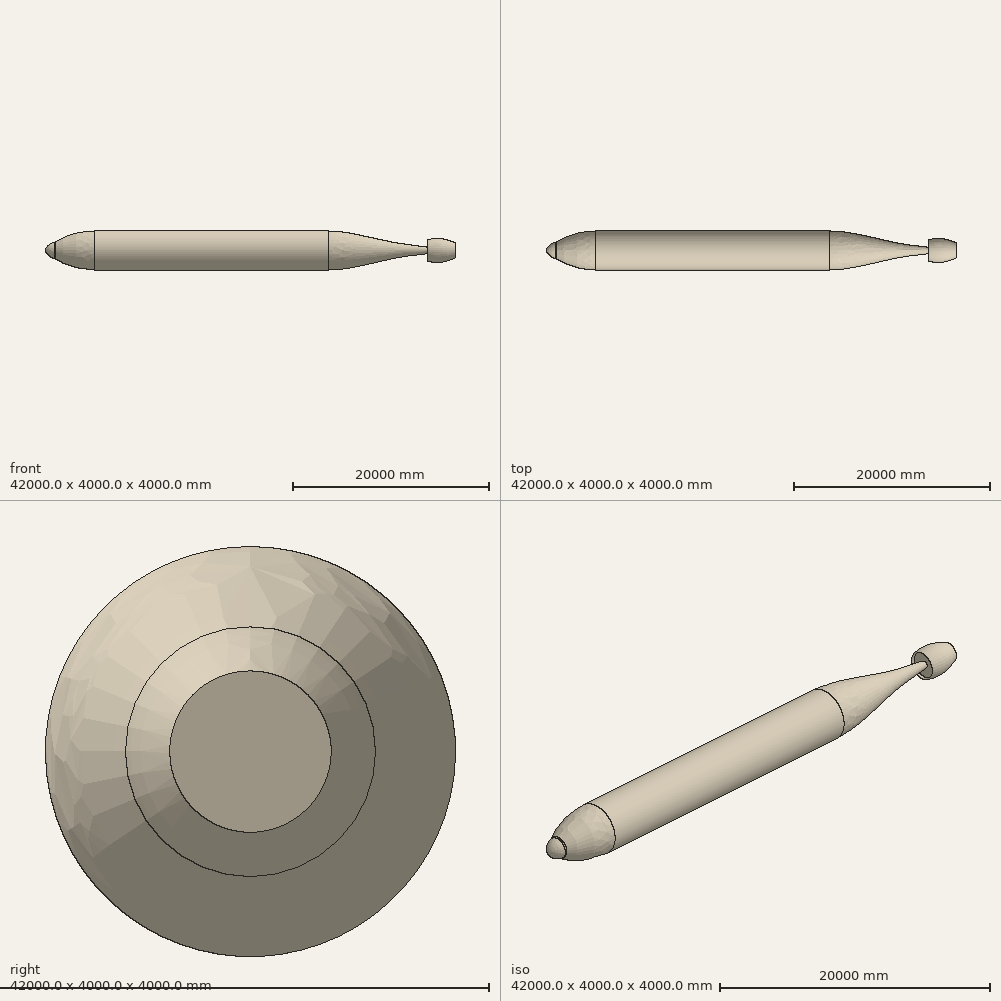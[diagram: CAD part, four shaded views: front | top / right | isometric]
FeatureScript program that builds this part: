
annotation { "Feature Type Name" : "Feature", "Feature Type Description" : "" }
export const myFeature = defineFeature(function(context is Context, id is Id, definition is map)
    precondition{}
    {
        {
            var Q0;
            Q0=qCreatedBy(makeId("Front.planeOp"),FACE);
            var sketch = newSketch(context, id + "F0", { "sketchPlane" : qUnion([Q0])});
            skLineSegment(sketch, "E0", {"start": v(5000, 2000) * mm, "end": v(22000, 2000) * mm});
            skLineSegment(sketch, "E1", {"start": v(0, 0) * mm, "end": v(42000, 0) * mm});
            skLineSegment(sketch, "E2", {"start": v(42000, 0) * mm, "end": v(42000, 787.4) * mm});
            skLineSegment(sketch, "E3", {"start": v(39430, 300) * mm, "end": v(39430, 1030) * mm});
            skFitSpline(sketch, "E4", {"points": [v(39430, 1030) * mm, v(39180, 1084.72) * mm, v(39645.76, 1187.8) * mm, v(40632.3, 1192.7) * mm, v(42000, 787.4) * mm], "startDerivative": vector(-3131.14, -53.02) * mm, "endDerivative": vector(4486.4, -1960.56) * mm});
            skFitSpline(sketch, "E5", {"points": [v(1059.75, 874.19) * mm, v(5000, 2000) * mm], "startDerivative": vector(1409.44, 924) * mm, "endDerivative": vector(6379.56, 131.88) * mm});
            skFitSpline(sketch, "E6", {"points": [v(1059.75, 874.19) * mm, v(947.74, 830.63) * mm], "startDerivative": vector(-112, -84) * mm, "endDerivative": vector(-150.02, -25.74) * mm});
            skFitSpline(sketch, "E7", {"points": [v(947.74, 830.63) * mm, v(0, 0) * mm], "startDerivative": vector(-1716.04, -382.73) * mm, "endDerivative": vector(-214.58, -1044.41) * mm});
            skLineSegment(sketch, "E8", {"start": v(22000, 2000) * mm, "end": v(29000, 2000) * mm});
            skFitSpline(sketch, "E9", {"points": [v(29000, 2000) * mm, v(35540.57, 851.22) * mm, v(39430, 300) * mm], "startDerivative": vector(11301.86, 0) * mm, "endDerivative": vector(9313.24, -1113.07) * mm});
            skSolve(sketch);
        }
        {
            var Q0;
            Q0=makeQuery(id+"F0.imprint","IMPRINT",FACE,{"disambiguationData":[TD([[makeQuery(id+"F0.imprint","IMPRINT",EDGE,{"derivedFrom":sQuery(id+"F0.wireOp",EDGE,"E0")}),-1.0]])]});
            var Q1;
            Q1=sQuery(id+"F0.wireOp",EDGE,"E1");
            revolve(context, id + "F1", {"entities" : qUnion([Q0]), "axis" : qUnion([Q1]), "revolveType" : RevolveType.FULL});
        }
    });
